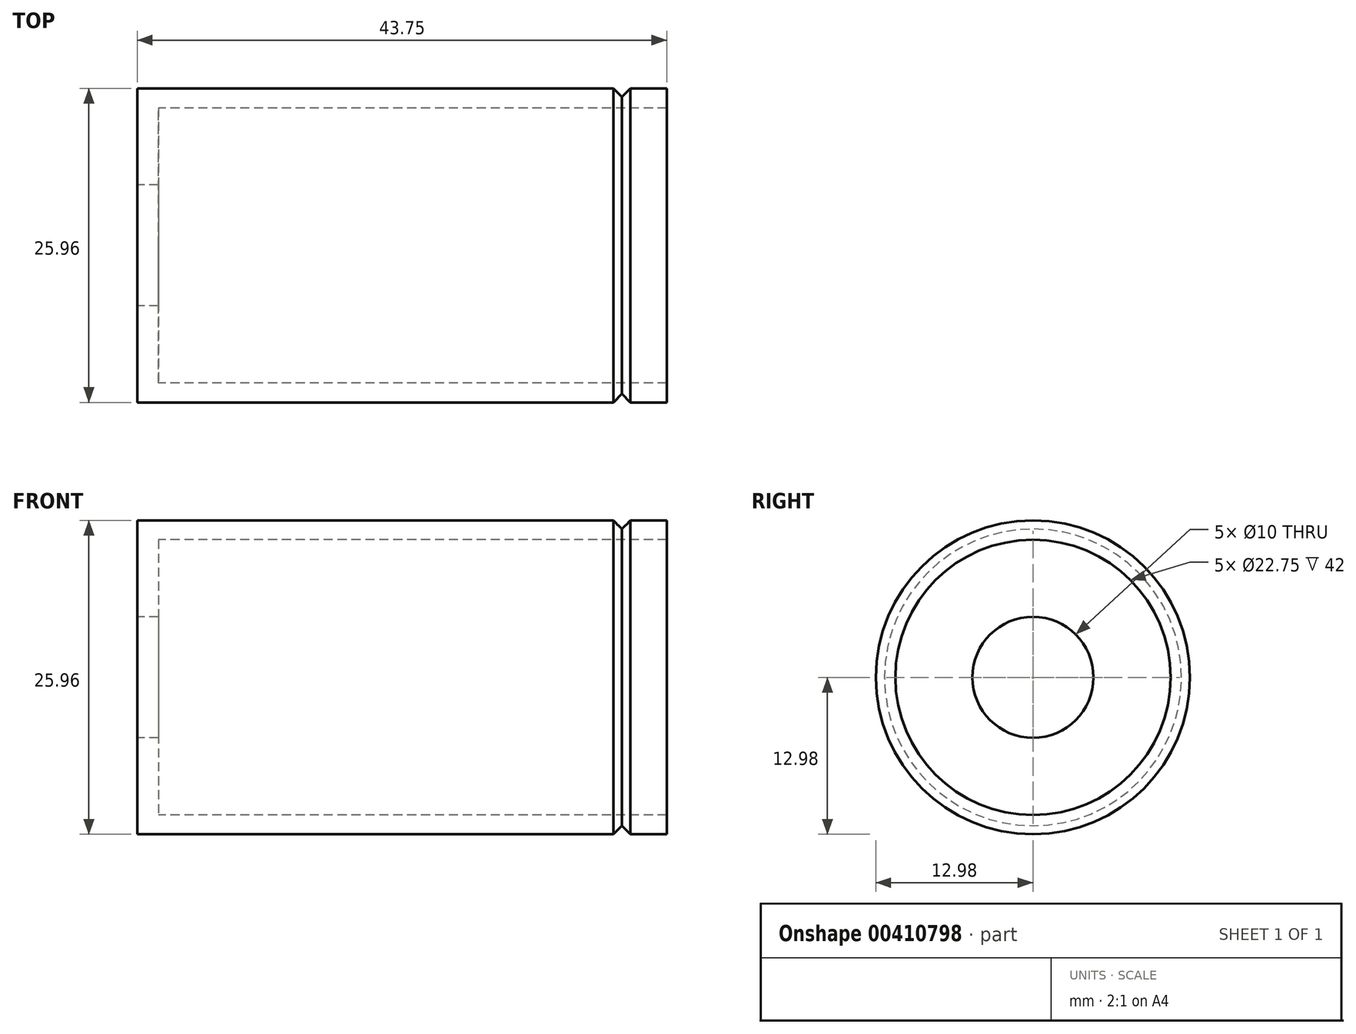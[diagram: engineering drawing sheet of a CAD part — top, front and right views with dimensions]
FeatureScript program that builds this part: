
annotation { "Feature Type Name" : "Feature", "Feature Type Description" : "" }
export const myFeature = defineFeature(function(context is Context, id is Id, definition is map)
    precondition{}
    {
        {
            var Q0;
            Q0=qCreatedBy(makeId("Front.planeOp"),FACE);
            var sketch = newSketch(context, id + "F0", { "sketchPlane" : qUnion([Q0])});
            skLineSegment(sketch, "E0", {"start": v(-16.6, 12.98) * mm, "end": v(22.73, 12.97) * mm});
            skLineSegment(sketch, "E1", {"start": v(-14.86, 11.38) * mm, "end": v(27.14, 11.37) * mm});
            skLineSegment(sketch, "E2", {"start": v(27.14, 11.37) * mm, "end": v(27.14, 12.97) * mm});
            skLineSegment(sketch, "E3", {"start": v(27.14, 12.97) * mm, "end": v(24.14, 12.97) * mm});
            skLineSegment(sketch, "E4", {"start": v(22.73, 12.97) * mm, "end": v(23.44, 12.27) * mm});
            skLineSegment(sketch, "E5", {"start": v(23.44, 12.27) * mm, "end": v(24.14, 12.97) * mm});
            skLineSegment(sketch, "E6", {"start": v(-31.75, 0) * mm, "end": v(38.44, 0) * mm, "construction": true});
            skLineSegment(sketch, "E7", {"start": v(-16.6, 12.98) * mm, "end": v(-16.6, 5) * mm});
            skLineSegment(sketch, "E8", {"start": v(-16.6, 5) * mm, "end": v(-14.86, 5) * mm});
            skLineSegment(sketch, "E9", {"start": v(-14.86, 5) * mm, "end": v(-14.86, 11.38) * mm});
            skSolve(sketch);
        }
        {
            var Q0;
            Q0=makeQuery(id+"F0.imprint","IMPRINT",FACE,{"disambiguationData":[TD([[makeQuery(id+"F0.imprint","IMPRINT",EDGE,{"derivedFrom":sQuery(id+"F0.wireOp",EDGE,"E0")}),-1.0]])]});
            var Q1;
            Q1=sQuery(id+"F0.wireOp",EDGE,"E6");
            revolve(context, id + "F1", {"entities" : qUnion([Q0]), "axis" : qUnion([Q1]), "revolveType" : RevolveType.FULL});
        }
    });
